# Revit family: DOT SINGLE HEAD RAIL 646_DTM30W6.5.24
name_source: partatom
category: Luminarias
units: mm (PartAtom-declared; Revit-internal decimal feet)

## family parameters
Compartido = No
Corte con vacíos al cargar = No
Cota de conector redondo = Diámetro de uso
Origen de luz = Sí
Punto de cálculo de habitación = No
Se basa en plano de trabajo = Sí
Siempre vertical = Sí
Tipo de pieza = Normal

## types (1)
- DOT SINGLE HEAD RAIL 646_DTM30W6.5.24
    Archivo de red fotométrica = L646A-30W-830-B-24_IESNA95.IES
    Cambio de temperatura de color de luz atenuada = <Ninguno>
    Comentarios de vataje = 90-240V
    Descripción = LUMINARIA DOWNLIGHT EN FORMATO RECTANGULAR COMPATIBLE CON RIEL DE 6 ENTRADAS Y 3 CIRCUITOS CON CABEZAL PARA PODER DIRIGIR LA LUMINARIA HASTA 30 GRADOS, CUERPO DE ALUMINIO ACABADO EN COLOR NEGRO, IP 20, PESO 1.48Kg, TIPO DE LED 3030SMD PHILIPS CON 30W TOTAL, 1400 LUMENES, 85LM/W, IRC 90, TEMPERATURA EN BLANCO CALIDO 3000K, 50 MIL HORAS DE VIDA PROMEDIO, APERTURA DE 24 GRADOS EN STOCK, ALIMENTADO A 90-240V
    Elevación por defecto = 1219 mm
    Fabricante = BRILLANT
    Filtro de color = 16777215
    Lámpara = 3030SMD PHILIPS
    Modelo = DTM30W6.5.24
    Watt per fixture = 30
    Ángulo de inclinación = 60.00°

## geometry (parser evidence)
native form markers: Blend x2
no freeform markers — native parametric forms only
